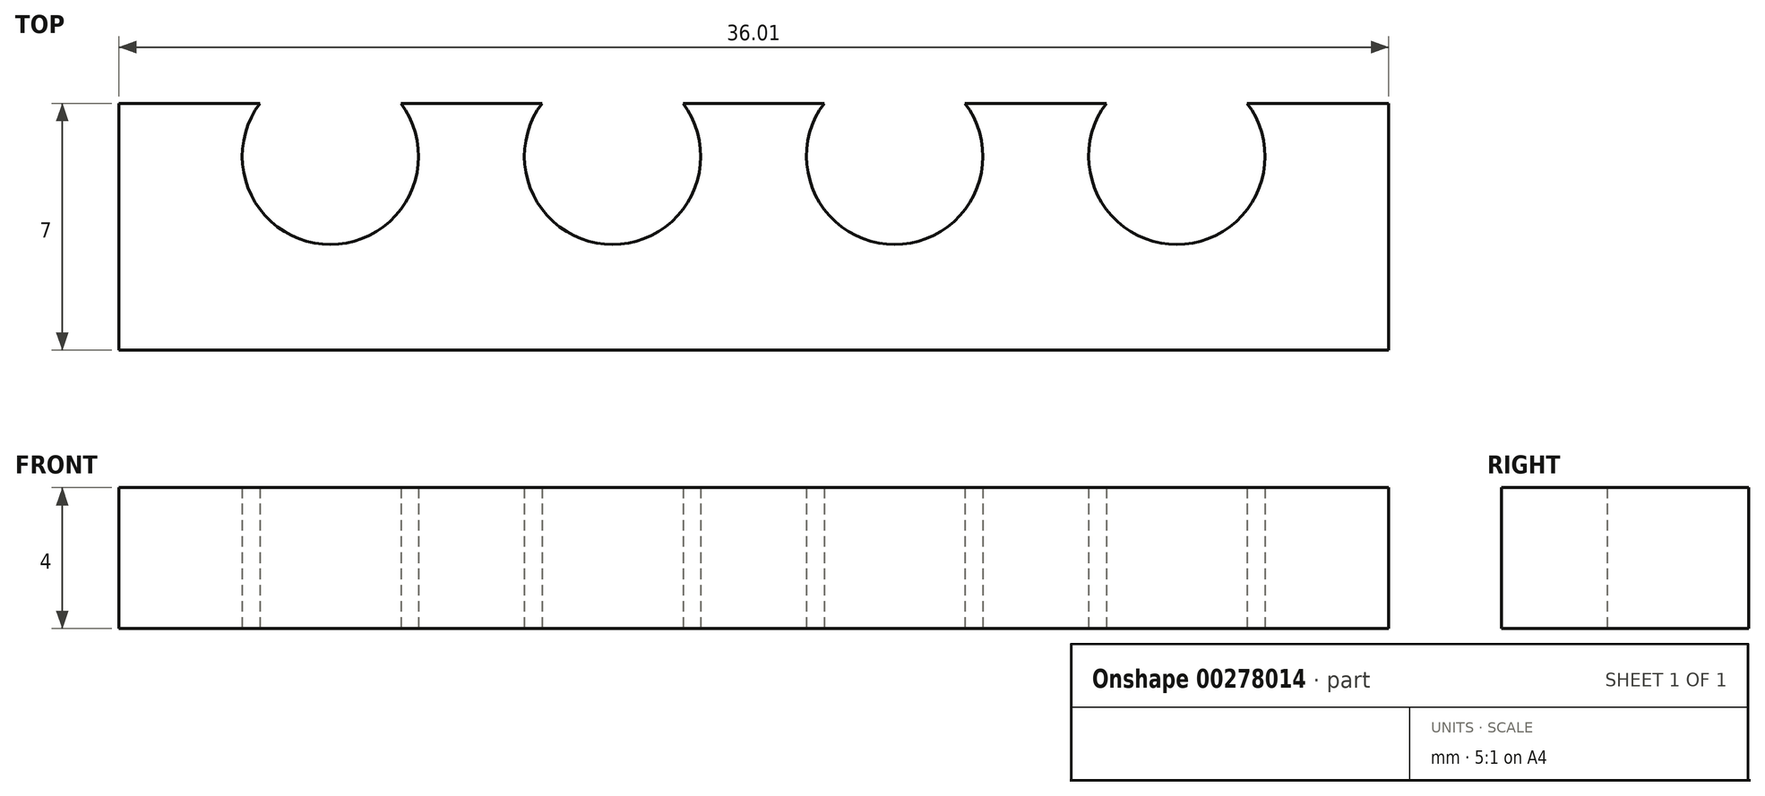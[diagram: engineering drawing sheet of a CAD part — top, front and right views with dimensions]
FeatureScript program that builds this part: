
annotation { "Feature Type Name" : "Feature", "Feature Type Description" : "" }
export const myFeature = defineFeature(function(context is Context, id is Id, definition is map)
    precondition{}
    {
        {
            var Q0;
            Q0=qCreatedBy(makeId("Top.planeOp"),FACE);
            var sketch = newSketch(context, id + "F0", { "sketchPlane" : qUnion([Q0])});
            skArc(sketch, "E0", {"start": v(4, 7) * mm, "mid": v(6, 3) * mm, "end": v(8, 7) * mm});
            skArc(sketch, "E1", {"start": v(12, 7) * mm, "mid": v(14, 3) * mm, "end": v(16, 7) * mm});
            skArc(sketch, "E2", {"start": v(20, 7) * mm, "mid": v(22, 3) * mm, "end": v(24, 7) * mm});
            skArc(sketch, "E3", {"start": v(28, 7) * mm, "mid": v(30, 3) * mm, "end": v(32, 7) * mm});
            skLineSegment(sketch, "E4", {"start": v(4, 7) * mm, "end": v(0, 7) * mm});
            skLineSegment(sketch, "E5", {"start": v(0, 7) * mm, "end": v(0, 0) * mm});
            skLineSegment(sketch, "E6", {"start": v(0, 0) * mm, "end": v(36, 0) * mm});
            skLineSegment(sketch, "E7", {"start": v(36, 0) * mm, "end": v(36, 7) * mm});
            skLineSegment(sketch, "E8", {"start": v(36, 7) * mm, "end": v(32, 7) * mm});
            skLineSegment(sketch, "E9", {"start": v(6, 5.5) * mm, "end": v(3.5, 5.5) * mm, "construction": true});
            skLineSegment(sketch, "E10", {"start": v(6, 5.5) * mm, "end": v(4, 7) * mm, "construction": true});
            skLineSegment(sketch, "E11", {"start": v(28, 7) * mm, "end": v(24, 7) * mm});
            skLineSegment(sketch, "E12", {"start": v(20, 7) * mm, "end": v(16, 7) * mm});
            skLineSegment(sketch, "E13", {"start": v(12, 7) * mm, "end": v(8, 7) * mm});
            skLineSegment(sketch, "E14", {"start": v(8.5, 5.5) * mm, "end": v(11.5, 5.5) * mm, "construction": true});
            skLineSegment(sketch, "E15", {"start": v(6, 3) * mm, "end": v(6, 0) * mm, "construction": true});
            skSolve(sketch);
        }
        {
            var Q0;
            Q0 = qSketchRegion(id + "F0", true);
            extrude(context, id + "F1", {"entities" : qUnion([Q0]), "depth" : 4 * mm});
        }
    });
